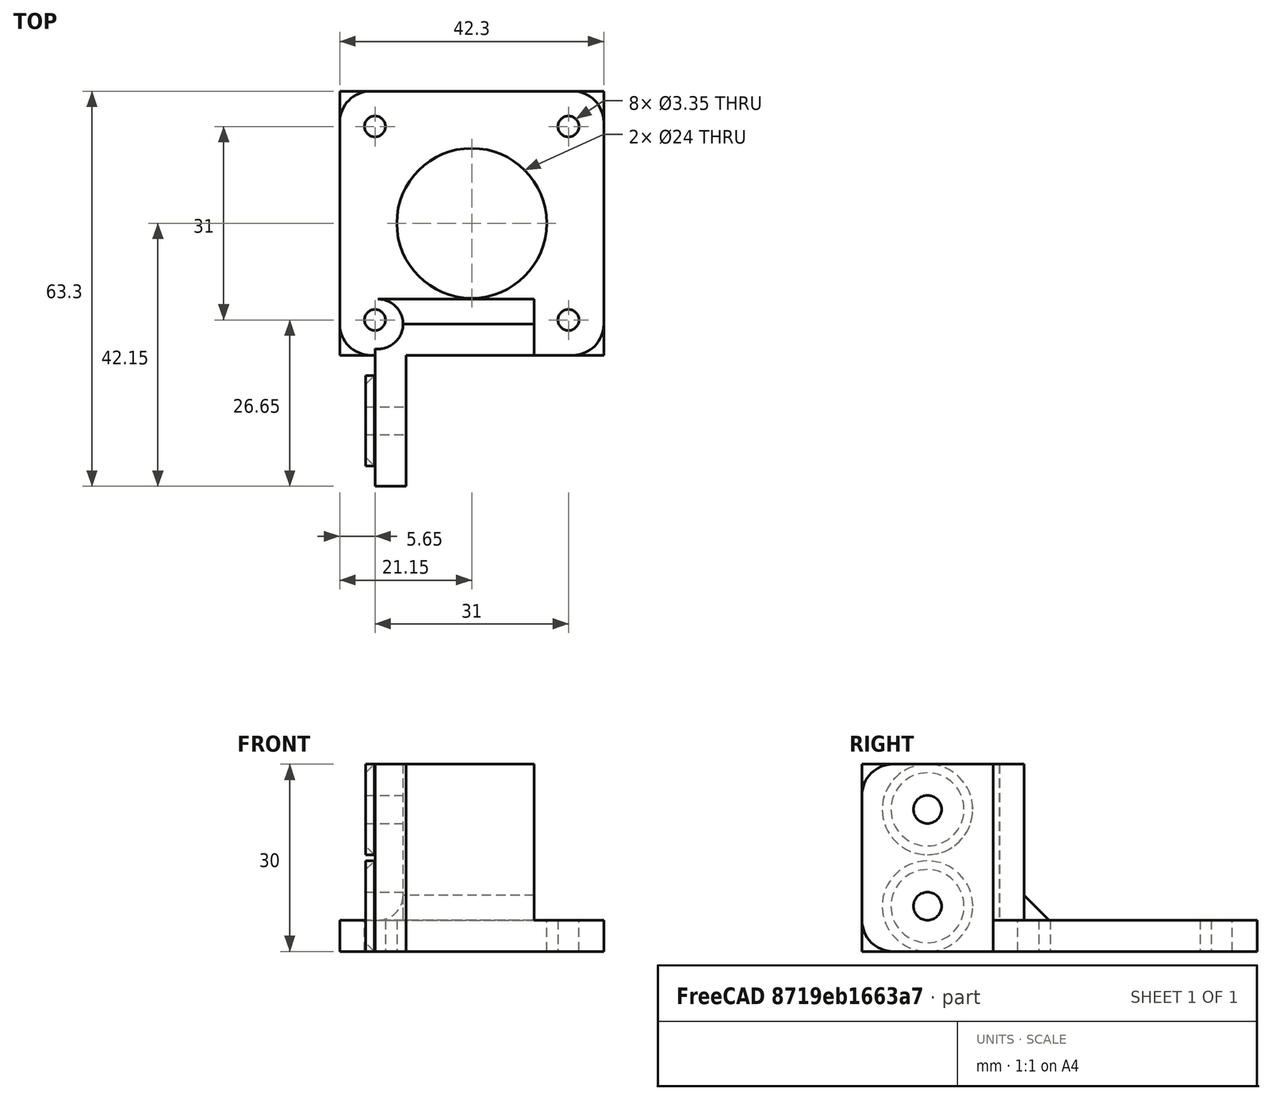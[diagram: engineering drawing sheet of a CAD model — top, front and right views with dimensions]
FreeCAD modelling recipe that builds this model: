
FCSTD DOCUMENT  (FreeCAD 0.19R24267 +99 (Git))
Label: monturaMotorZ
License: All rights reserved
LicenseURL: http://en.wikipedia.org/wiki/All_rights_reserved
objects: Part::Fuse×9, Part::Cylinder×7, Part::Fillet×6, Part::Part2DObjectPython×5, Part::Box×4, Part::Cut×3, Part::Chamfer×3, Part::MultiFuse×2, Part::FeaturePython×1, Part::Extrusion×1, Part::Refine×1
note: 42 computed .brp shape members not serialized (recipe doc carries the construction recipe); baked Part::Feature solids carry a one-line shape summary decoded from their .brp

FEATURE [Part::Box] cube
  AttacherType = Attacher::AttachEngine3D
  Height = 5
  Length = 42.3
  Width = 42.3
FEATURE [Part::Part2DObjectPython] circle  # Draft 2D object (typed FeaturePython)
  Area = 452.389
  FirstAngle = 0
  LastAngle = 0
  MakeFace = true
  Radius = 12
FEATURE [Part::Part2DObjectPython] circle001  # Draft 2D object (typed FeaturePython)
  Area = 8.81413
  FirstAngle = 0
  LastAngle = 0
  MakeFace = true
  Placement = pos=(15.5,15.5,0) rot=(0,0,1;0rad)
  Radius = 1.675
FEATURE [Part::Part2DObjectPython] circle002  # Draft 2D object (typed FeaturePython)
  Area = 8.81413
  FirstAngle = 0
  LastAngle = 0
  MakeFace = true
  Placement = pos=(-15.5,15.5,0) rot=(0,0,1;1.5708rad)
  Radius = 1.675
FEATURE [Part::Part2DObjectPython] circle003  # Draft 2D object (typed FeaturePython)
  Area = 8.81413
  FirstAngle = 0
  LastAngle = 0
  MakeFace = true
  Placement = pos=(-15.5,-15.5,0) rot=(0,0,1;3.14159rad)
  Radius = 1.675
FEATURE [Part::Part2DObjectPython] circle004  # Draft 2D object (typed FeaturePython)
  Area = 8.81413
  FirstAngle = 0
  LastAngle = 0
  MakeFace = true
  Placement = pos=(15.5,-15.5,0) rot=(0,0,-1;1.5708rad)
  Radius = 1.675
FEATURE [Part::MultiFuse] Group
  Shapes = -> [circle001,circle002,circle003,circle004]
FEATURE [Part::Fuse] Group001
  Base = -> circle
  Tool = -> Group
FEATURE [Part::FeaturePython] RefineLinearExtrude  # WARN: FeaturePython — macro-defined, semantics opaque (R4)
  Base = -> Group001
FEATURE [Part::Extrusion] LinearExtrude
  Base = -> RefineLinearExtrude
  Dir = (0,0,20)
  DirMode = 0
  FaceMakerClass = Part::FaceMakerBullseye
  LengthFwd = 0
  LengthRev = 0
  Placement = pos=(21.15,21.15,-10) rot=(0,0,1;0rad)
  Solid = false
  Symmetric = false
FEATURE [Part::Cut] difference
  Base = -> cube
  Tool = -> LinearExtrude
FEATURE [Part::Box] cube001
  AttacherType = Attacher::AttachEngine3D
  Height = 26
  Length = 30
  Placement = pos=(-15,-15.5,-13) rot=(0,0,1;0rad)
  Width = 31
FEATURE [Part::Box] cube002
  AttacherType = Attacher::AttachEngine3D
  Height = 21
  Length = 60
  Placement = pos=(-30,-10.5,-13) rot=(0,0,1;0rad)
  Width = 21
FEATURE [Part::Cylinder] cylinder
  Angle = 360
  AttacherType = Attacher::AttachEngine3D
  Height = 200
  Placement = pos=(-100,15,13) rot=(0.57735,0.57735,0.57735;2.0944rad)
  Radius = 4
FEATURE [Part::Fuse] union
  Base = -> cube002
  Tool = -> cylinder
FEATURE [Part::Cut] difference001
  Base = -> cube001
  Placement = pos=(10,0,-13) rot=(0,0,1;0rad)
  Tool = -> union
FEATURE [Part::Cylinder] cylinder001
  Angle = 360
  AttacherType = Attacher::AttachEngine3D
  Height = 6.5
  Placement = pos=(0,0,0) rot=(1,0,0;1.5708rad)
  Radius = 7.25
FEATURE [Part::Cylinder] cylinder002
  Angle = 360
  AttacherType = Attacher::AttachEngine3D
  Height = 6.5
  Placement = pos=(15.5,0,0) rot=(1,0,0;1.5708rad)
  Radius = 7.25
FEATURE [Part::Fuse] Group002
  Base = -> cylinder001
  Placement = pos=(2.25,-10.5,-15.5) rot=(0,0,1;0rad)
  Tool = -> cylinder002
FEATURE [Part::Cylinder] cylinder003
  Angle = 360
  AttacherType = Attacher::AttachEngine3D
  Height = 6.5
  Placement = pos=(0,0,0) rot=(1,0,0;1.5708rad)
  Radius = 7.25
FEATURE [Part::Cylinder] cylinder004
  Angle = 360
  AttacherType = Attacher::AttachEngine3D
  Height = 6.5
  Placement = pos=(15.5,0,0) rot=(1,0,0;1.5708rad)
  Radius = 7.25
FEATURE [Part::Fuse] Group003
  Base = -> cylinder003
  Placement = pos=(2.25,10.5,-15.5) rot=(1,0,0;3.14159rad)
  Tool = -> cylinder004
FEATURE [Part::Fuse] Group004
  Base = -> Group002
  Tool = -> Group003
FEATURE [Part::Fuse] union001
  Base = -> difference001
  Tool = -> Group004
FEATURE [Part::Cylinder] cylinder005
  Angle = 360
  AttacherType = Attacher::AttachEngine3D
  Height = 1000
  Placement = pos=(0,500,0) rot=(1,0,0;1.5708rad)
  Radius = 2.25
FEATURE [Part::Cylinder] cylinder006
  Angle = 360
  AttacherType = Attacher::AttachEngine3D
  Height = 1000
  Placement = pos=(15.5,500,0) rot=(1,0,0;1.5708rad)
  Radius = 2.25
FEATURE [Part::Fuse] Group005
  Base = -> cylinder005
  Placement = pos=(2.25,0,-15.5) rot=(0,0,1;0rad)
  Tool = -> cylinder006
FEATURE [Part::Box] cube003
  AttacherType = Attacher::AttachEngine3D
  Height = 500
  Length = 500
  Placement = pos=(-250,-510,-250) rot=(0,0,1;0rad)
  Width = 500
FEATURE [Part::Fuse] union002
  Base = -> Group005
  Tool = -> cube003
FEATURE [Part::Cut] difference002
  Base = -> union001
  Placement = pos=(21.15,5,25) rot=(-0.57735,0.57735,0.57735;2.0944rad)
  Tool = -> union002
FEATURE [Part::Fuse] Group006
  Base = -> difference
  Tool = -> difference002
FEATURE [Part::MultiFuse] Fusion
  Shapes = -> [difference,difference002]
FEATURE [Part::Refine] Fusion001
  Source = -> Fusion
FEATURE [Part::Chamfer] Chamfer
  Base = -> Fusion001
  Edges = 1 edges r=4: [Edge12]
FEATURE [Part::Chamfer] Chamfer001
  Base = -> Chamfer
  Edges = 1 edges r=1.4: [Edge65]
FEATURE [Part::Chamfer] Chamfer002
  Base = -> Chamfer001
  Edges = 1 edges r=1.4: [Edge55]
FEATURE [Part::Fillet] Fillet
  Base = -> Chamfer002
  Edges = 1 edges r=5: [Edge29]
FEATURE [Part::Fillet] Fillet001
  Base = -> Fillet
  Edges = 1 edges r=5: [Edge15]
FEATURE [Part::Fillet] Fillet002
  Base = -> Fillet001
  Edges = 1 edges r=5: [Edge38]
FEATURE [Part::Fillet] Fillet003
  Base = -> Fillet002
  Edges = 1 edges r=5: [Edge37]
FEATURE [Part::Fillet] Fillet004
  Base = -> Fillet003
  Edges = 1 edges r=5: [Edge19]
FEATURE [Part::Fillet] Fillet005
  Base = -> Fillet004
  Edges = 1 edges r=5: [Edge25]
